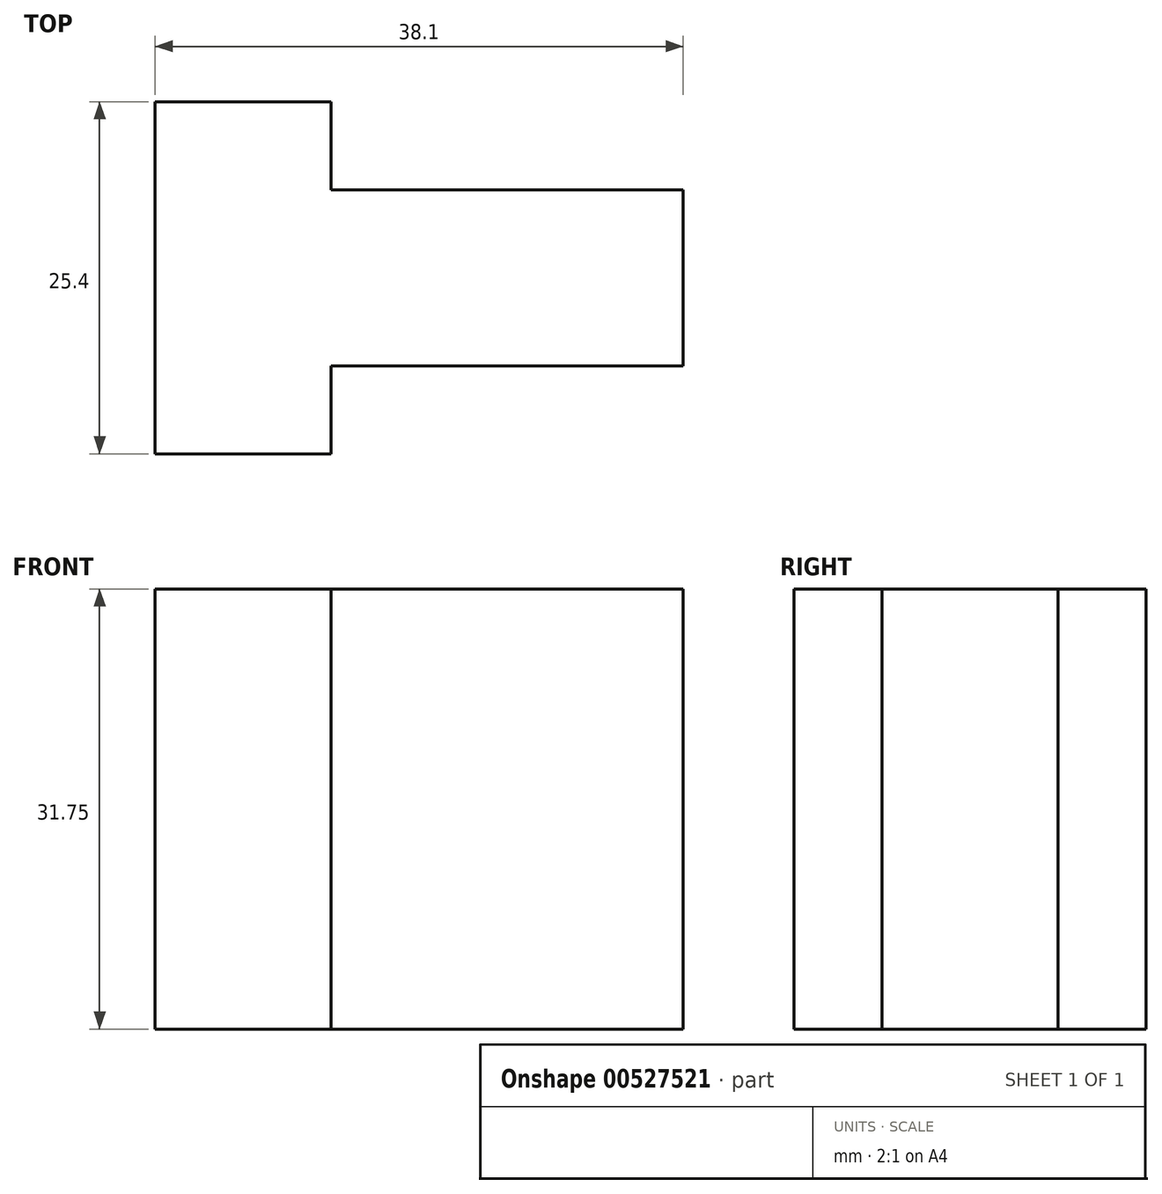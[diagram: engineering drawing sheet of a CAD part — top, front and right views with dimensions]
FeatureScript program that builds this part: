
annotation { "Feature Type Name" : "Feature", "Feature Type Description" : "" }
export const myFeature = defineFeature(function(context is Context, id is Id, definition is map)
    precondition{}
    {
        {
            var Q0;
            Q0=qCreatedBy(makeId("Top.planeOp"),FACE);
            var sketch = newSketch(context, id + "F0", { "sketchPlane" : qUnion([Q0])});
            skLineSegment(sketch, "E0", {"start": v(0, 0) * mm, "end": v(12.7, 0) * mm});
            skLineSegment(sketch, "E1", {"start": v(12.7, 0) * mm, "end": v(12.7, 6.35) * mm});
            skLineSegment(sketch, "E2", {"start": v(12.7, 6.35) * mm, "end": v(38.1, 6.35) * mm});
            skLineSegment(sketch, "E3", {"start": v(38.1, 6.35) * mm, "end": v(38.1, 19.05) * mm});
            skLineSegment(sketch, "E4", {"start": v(38.1, 19.05) * mm, "end": v(12.7, 19.05) * mm});
            skLineSegment(sketch, "E5", {"start": v(12.7, 19.05) * mm, "end": v(12.7, 25.4) * mm});
            skLineSegment(sketch, "E6", {"start": v(12.7, 25.4) * mm, "end": v(0, 25.4) * mm});
            skLineSegment(sketch, "E7", {"start": v(0, 25.4) * mm, "end": v(0, 0) * mm});
            skSolve(sketch);
        }
        {
            var Q0;
            Q0=makeQuery(id+"F0.imprint","IMPRINT",FACE,{"disambiguationData":[TD([[makeQuery(id+"F0.imprint","IMPRINT",EDGE,{"derivedFrom":sQuery(id+"F0.wireOp",EDGE,"E0")}),1.0]])]});
            extrude(context, id + "F1", {"entities" : qUnion([Q0]), "depth" : 31.75 * mm, "offsetDistance" : 25.4 * mm});
        }
    });
